# Revit family: Legrand Colonnes clippage direct
name_source: partatom
category: Installations électriques
units: mm (PartAtom-declared; Revit-internal decimal feet)

## family parameters
Basée sur le plan de construction = Non
Conserver l'orientation des annotations = Non
Cote de connecteur circulaire = Utiliser le diamètre
Couper avec des vides une fois chargée = Oui
Partagée = Non
Point de calcul de pièce = Non
Toujours verticalement = Oui
Type d'élément = Normal

## types (10) — shared parameters
Fabricant = LEGRAND
Standard = A clippage direct-ON
zero-valued in all types: Elévation par défaut

## per-type parameters (varying)
| type | 1 CPT | 2 CPT | 4 CPT | Description | Finition | H1 | HC | Kit de finition perche | Largeur | Longueur | Matériau couvercle | Matériau principal | Matériaux corps | Modèle | Nombre de compartiments | Séparateur |
| Colonne 1 cpt CV45 2,67M Blanc | Oui | Non | Non | Colonne a clippage direct 1 compartiment 2,670m Blanc | Blanc | 2700 mm | 2660 mm  [stored 8.72703 ft] | Kit de finition perche : Kit finition perche PVC Blanc | 75 mm | 82 mm | Legrand - Plastique blanc | Aluminium | Legrand - Aluminium blanc | LG-653010 | 1 compartiment | 35 mm  [stored 0.114829 ft] |
| Colonne 1 cpt CV45 2,67M Noir | Oui | Non | Non | Colonne a clippage direct 1 compartiment 2,67m Noir | Noir | 2700 mm | 2660 mm  [stored 8.72703 ft] | Kit de finition perche : Kit finition perche PVC Noir | 75 mm | 82 mm | Legrand - Plastique noir | Aluminium | Legrand - Aluminium noir | LG-653012 | 1 compartiment | 35 mm  [stored 0.114829 ft] |
| Colonne 1 cpt CV45 3,92M Blanc | Oui | Non | Non | Colonne a clippage direct 1 compartiment 3,92m Blanc | Blanc | 3900 mm | 3860 mm | Kit de finition perche : Kit finition perche PVC Blanc | 75 mm | 82 mm | Legrand - Plastique blanc | Aluminium | Legrand - Aluminium blanc | LG-653013 | 1 compartiment | 35 mm  [stored 0.114829 ft] |
| Colonne 1 cpt CV45 3,92M Noir | Oui | Non | Non | Colonne a clippage direct 1 compartiment 3,92m Noir | Noir | 3900 mm | 3860 mm | Kit de finition perche : Kit finition perche PVC Noir | 75 mm | 82 mm | Legrand - Plastique noir | Aluminium | Legrand - Aluminium noir | LG-653015 | 1 compartiment | 35 mm  [stored 0.114829 ft] |
| Colonne 2 cpts 45 2,67M Blanc | Non | Oui | Non | Colonne a clippage direct 2 compartiments 2,67m Blanc | Blanc | 2700 mm | 2660 mm  [stored 8.72703 ft] | Kit de finition perche : Kit finition perche PVC Blanc | 75 mm | 125 mm  [stored 0.410105 ft] | Legrand - Plastique blanc | Plastique | Legrand - Plastique blanc | LG-653030 | 2 compartiments | 35 mm  [stored 0.114829 ft] |
| Colonne 2 cpts 45 2,67M Noir | Non | Oui | Non | Colonne a clippage direct 2 compartiments 2,67m Noir | Noir | 2700 mm | 2660 mm  [stored 8.72703 ft] | Kit de finition perche : Kit finition perche PVC Noir | 75 mm | 125 mm  [stored 0.410105 ft] | Legrand - Plastique noir | Aluminium | Legrand - Aluminium noir | LG-653032 | 2 compartiments | 35 mm  [stored 0.114829 ft] |
| Colonne 2 cpts 45 3,92M Blanc | Non | Oui | Non | Colonne a clippage direct 2 compartiments 3,92m Blanc | Blanc | 3900 mm | 3860 mm | Kit de finition perche : Kit finition perche PVC Blanc | 75 mm | 125 mm  [stored 0.410105 ft] | Legrand - Plastique blanc | Plastique | Legrand - Plastique blanc | LG-653033 | 2 compartiments | 35 mm  [stored 0.114829 ft] |
| Colonne 2 cpts 45 3,92M Noir | Non | Oui | Non | Colonne a clippage direct 2 compartiments 3,92m Noir | Noir | 3900 mm | 3860 mm | Kit de finition perche : Kit finition perche PVC Noir | 75 mm | 125 mm  [stored 0.410105 ft] | Legrand - Plastique noir | Aluminium | Legrand - Aluminium noir | LG-653035 | 2 compartiments | 35 mm  [stored 0.114829 ft] |
| Colonne 4 cpts 45 2,67M Blanc | Non | Non | Oui | Colonne a clippage direct 4 compartiments 2,670m Blanc | Blanc | 680 mm  [stored 2.23097 ft] | 640 mm  [stored 2.09974 ft] | Kit de finition perche : Kit finition perche PVC Blanc | 125 mm  [stored 0.410105 ft] | 125 mm  [stored 0.410105 ft] | Legrand - Plastique blanc | Aluminium | Legrand - Aluminium blanc | LG-653050 | 4 compartiments | 125 mm  [stored 0.410105 ft] |
| Colonne 4 cpts 45 2,67M Noir | Non | Non | Oui | Colonne a clippage direct 4 compartiments 2,670m Noir | Noir | 680 mm  [stored 2.23097 ft] | 640 mm  [stored 2.09974 ft] | Kit de finition perche : Kit finition perche PVC Noir | 125 mm  [stored 0.410105 ft] | 125 mm  [stored 0.410105 ft] | Legrand - Plastique noir | Aluminium | Legrand - Aluminium noir | LG-653052 | 4 compartiments | 125 mm  [stored 0.410105 ft] |

note: [stored X ft] marks values corroborated as IEEE doubles in the binary element streams (Revit-internal decimal feet)
